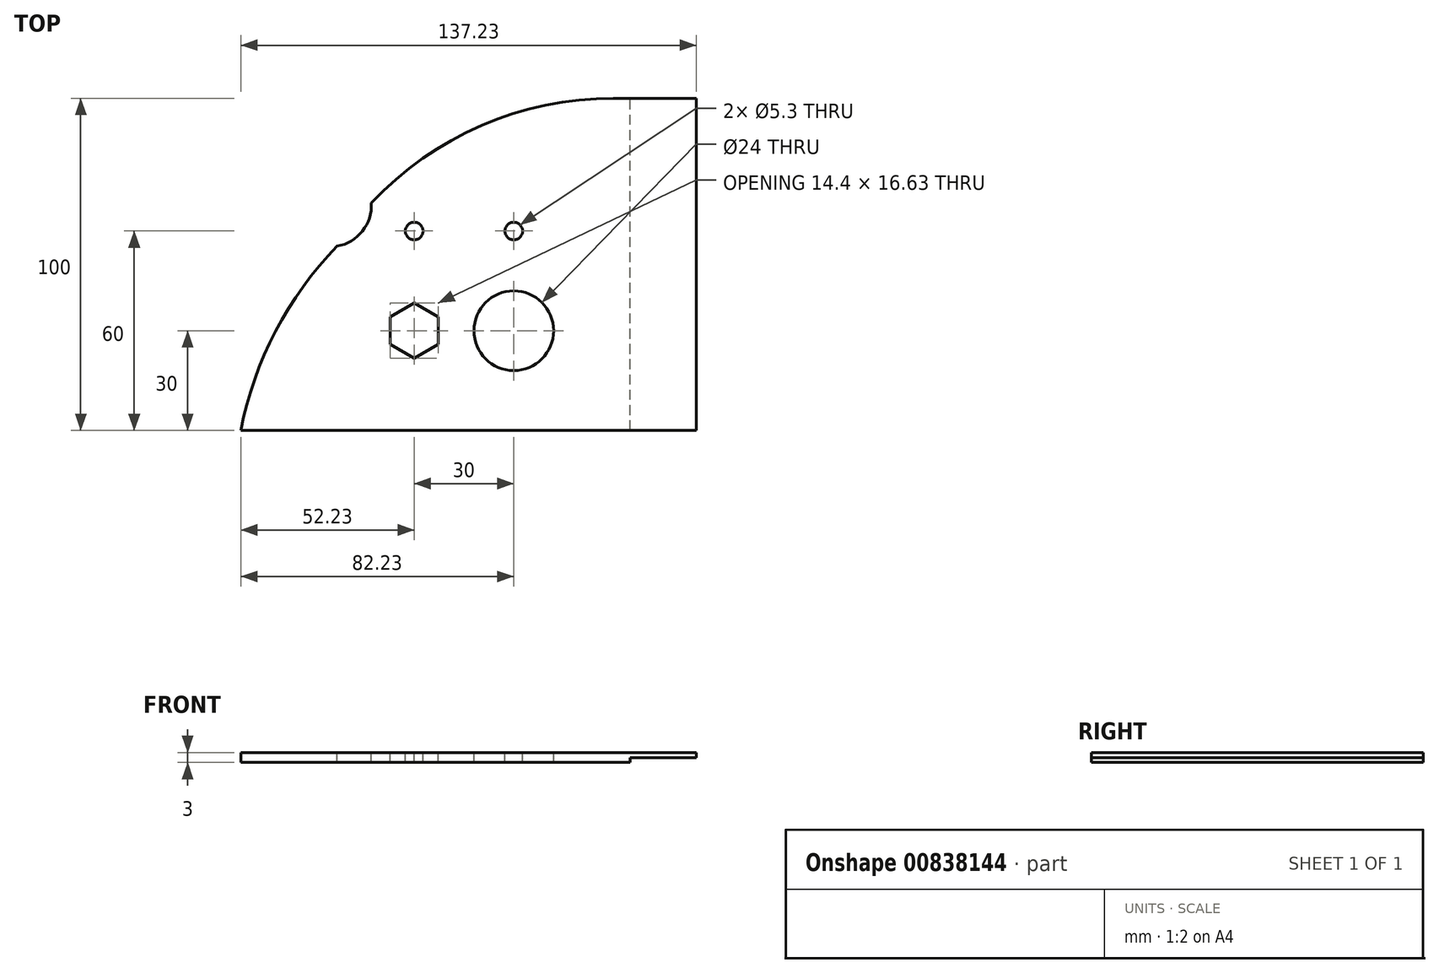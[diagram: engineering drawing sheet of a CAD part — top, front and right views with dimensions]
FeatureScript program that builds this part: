
annotation { "Feature Type Name" : "Feature", "Feature Type Description" : "" }
export const myFeature = defineFeature(function(context is Context, id is Id, definition is map)
    precondition{}
    {
        {
            var Q0;
            Q0=qCreatedBy(makeId("Top.planeOp"),FACE);
            var sketch = newSketch(context, id + "F0", { "sketchPlane" : qUnion([Q0])});
            skLineSegment(sketch, "E0", {"start": v(-202.23, 0) * mm, "end": v(-197.81, 20.8) * mm});
            skLineSegment(sketch, "E1", {"start": v(216.1, 0) * mm, "end": v(-202.23, 0) * mm});
            skLineSegment(sketch, "E2", {"start": v(-100, 100) * mm, "end": v(100, 100) * mm});
            skArc(sketch, "E3", {"start": v(-100, 100) * mm, "mid": v(-162.93, 77.71) * mm, "end": v(-197.81, 20.8) * mm});
            skArc(sketch, "E4", {"start": v(209.29, 20.8) * mm, "mid": v(167.49, 78.12) * mm, "end": v(100, 100) * mm});
            skLineSegment(sketch, "E5", {"start": v(0, 100) * mm, "end": v(0, 0) * mm, "construction": true});
            skLineSegment(sketch, "E6", {"start": v(216.1, 0) * mm, "end": v(209.29, 20.8) * mm});
            skSolve(sketch);
        }
        {
            var Q0;
            Q0=qSketchRegion(id+"F0",true);
            extrude(context, id + "F1", {"entities" : qUnion([Q0]), "depth" : 3 * mm, "offsetDistance" : 25 * mm});
        }
        {
            var Q0;
            Q0=makeQuery(id+"F1.opExtrude","CAP_FACE",FACE,{"disambiguationData":[OSD([sQuery(id+"F0.wireOp",EDGE,"E0"),sQuery(id+"F0.wireOp",EDGE,"E1"),sQuery(id+"F0.wireOp",EDGE,"E2"),sQuery(id+"F0.wireOp",EDGE,"E3"),sQuery(id+"F0.wireOp",EDGE,"E4"),sQuery(id+"F0.wireOp",EDGE,"E6")])],"isStart":false});
            var sketch = newSketch(context, id + "F2", { "sketchPlane" : qUnion([Q0])});
            skCircle(sketch, "E7", {"center": v(0, 12.5) * mm, "radius": 12.6 * mm});
            skLineSegment(sketch, "E8", {"start": v(-11.1, 18.46) * mm, "end": v(-21.76, 0) * mm});
            skLineSegment(sketch, "E9", {"start": v(11.1, 18.46) * mm, "end": v(21.76, 0) * mm});
            skLineSegment(sketch, "E10", {"start": v(21.76, 0) * mm, "end": v(-21.76, 0) * mm});
            skSolve(sketch);
        }
        {
            var Q0;
            Q0=qSketchRegion(id+"F2",true);
            extrude(context, id + "F3", {"entities" : qUnion([Q0]), "operationType" : NewBodyOperationType.REMOVE, "oppositeDirection" : true, "depth" : 25 * mm, "offsetDistance" : 25 * mm});
        }
        {
            var Q0;
            Q0=makeQuery(id+"F3.boolean.opBoolean","COPY",EDGE,{"derivedFrom":makeQuery(id+"F3.opExtrude","SWEPT_EDGE",EDGE,{"disambiguationData":[OSD([sQuery(id+"F0.wireOp",EDGE,"E1"),sQuery(id+"F2.wireOp",EDGE,"E8"),sQuery(id+"F2.wireOp",EDGE,"E10")])]})});
            var Q1;
            Q1=makeQuery(id+"F3.boolean.opBoolean","COPY",EDGE,{"derivedFrom":makeQuery(id+"F3.opExtrude","SWEPT_EDGE",EDGE,{"disambiguationData":[OSD([sQuery(id+"F0.wireOp",EDGE,"E1"),sQuery(id+"F2.wireOp",EDGE,"E9"),sQuery(id+"F2.wireOp",EDGE,"E10")])]})});
            fillet(context, id + "F4", {"entities" : qUnion([Q0, Q1]), "radius" : 5 * mm, "tangentPropagation" : true, "allowEdgeOverflow" : false});
        }
        {
            var Q0;
            Q0=makeQuery(id+"F1.opExtrude","CAP_FACE",FACE,{"disambiguationData":[OSD([sQuery(id+"F0.wireOp",EDGE,"E0"),sQuery(id+"F0.wireOp",EDGE,"E1"),sQuery(id+"F0.wireOp",EDGE,"E2"),sQuery(id+"F0.wireOp",EDGE,"E3"),sQuery(id+"F0.wireOp",EDGE,"E4"),sQuery(id+"F0.wireOp",EDGE,"E6")])],"isStart":false});
            var sketch = newSketch(context, id + "F5", { "sketchPlane" : qUnion([Q0])});
            skCircle(sketch, "E11.cCircle", {"center": v(-160, 30) * mm, "radius": 8.31 * mm, "construction": true});
            skLineSegment(sketch, "E11.0", {"start": v(-167.2, 34.16) * mm, "end": v(-160, 38.31) * mm});
            skLineSegment(sketch, "E11.1", {"start": v(-160, 38.31) * mm, "end": v(-152.8, 34.16) * mm});
            skLineSegment(sketch, "E11.2", {"start": v(-152.8, 34.16) * mm, "end": v(-152.8, 25.84) * mm});
            skLineSegment(sketch, "E11.3", {"start": v(-152.8, 25.84) * mm, "end": v(-160, 21.69) * mm});
            skLineSegment(sketch, "E11.4", {"start": v(-160, 21.69) * mm, "end": v(-167.2, 25.84) * mm});
            skLineSegment(sketch, "E11.5", {"start": v(-167.2, 25.84) * mm, "end": v(-167.2, 34.16) * mm});
            skCircle(sketch, "E12", {"center": v(-130, 30) * mm, "radius": 12 * mm});
            skCircle(sketch, "E13", {"center": v(-130, 60) * mm, "radius": 2.65 * mm});
            skCircle(sketch, "E14", {"center": v(-160, 60) * mm, "radius": 2.65 * mm});
            skSolve(sketch);
        }
        {
            var Q0;
            Q0=qSketchRegion(id+"F5",true);
            extrude(context, id + "F6", {"entities" : qUnion([Q0]), "operationType" : NewBodyOperationType.REMOVE, "oppositeDirection" : true, "depth" : 25 * mm, "offsetDistance" : 25 * mm});
        }
        {
            var Q0;
            Q0=makeQuery(id+"F1.opExtrude","CAP_FACE",FACE,{"disambiguationData":[OSD([sQuery(id+"F0.wireOp",EDGE,"E0"),sQuery(id+"F0.wireOp",EDGE,"E1"),sQuery(id+"F0.wireOp",EDGE,"E2"),sQuery(id+"F0.wireOp",EDGE,"E3"),sQuery(id+"F0.wireOp",EDGE,"E4"),sQuery(id+"F0.wireOp",EDGE,"E6")])],"isStart":false});
            var sketch = newSketch(context, id + "F7", { "sketchPlane" : qUnion([Q0])});
            skLineSegment(sketch, "E15.bottom", {"start": v(-39, 30) * mm, "end": v(39, 30) * mm});
            skLineSegment(sketch, "E15.top", {"start": v(-39, 85.5) * mm, "end": v(39, 85.5) * mm});
            skLineSegment(sketch, "E15.left", {"start": v(-39, 30) * mm, "end": v(-39, 85.5) * mm});
            skLineSegment(sketch, "E15.right", {"start": v(39, 30) * mm, "end": v(39, 85.5) * mm});
            skCircle(sketch, "E16", {"center": v(-42.63, 28.25) * mm, "radius": 2 * mm});
            skCircle(sketch, "E17", {"center": v(-42.63, 87.25) * mm, "radius": 2 * mm});
            skCircle(sketch, "E18", {"center": v(42.37, 87.25) * mm, "radius": 2 * mm});
            skCircle(sketch, "E19", {"center": v(42.37, 28.25) * mm, "radius": 2 * mm});
            skLineSegment(sketch, "E20", {"start": v(0, 85.5) * mm, "end": v(0, 30) * mm, "construction": true});
            skSolve(sketch);
        }
        {
            var Q0;
            Q0=qSketchRegion(id+"F7",true);
            extrude(context, id + "F8", {"entities" : qUnion([Q0]), "operationType" : NewBodyOperationType.REMOVE, "oppositeDirection" : true, "depth" : 25 * mm, "offsetDistance" : 25 * mm});
        }
        {
            var Q0;
            Q0=makeQuery(id+"F1.opExtrude","CAP_FACE",FACE,{"disambiguationData":[OSD([sQuery(id+"F0.wireOp",EDGE,"E0"),sQuery(id+"F0.wireOp",EDGE,"E1"),sQuery(id+"F0.wireOp",EDGE,"E2"),sQuery(id+"F0.wireOp",EDGE,"E3"),sQuery(id+"F0.wireOp",EDGE,"E4"),sQuery(id+"F0.wireOp",EDGE,"E6")])],"isStart":false});
            var sketch = newSketch(context, id + "F9", { "sketchPlane" : qUnion([Q0])});
            skCircle(sketch, "E21", {"center": v(115, 30) * mm, "radius": 8.15 * mm});
            skSolve(sketch);
        }
        {
            var Q0;
            Q0=qSketchRegion(id+"F9",true);
            extrude(context, id + "F10", {"entities" : qUnion([Q0]), "operationType" : NewBodyOperationType.REMOVE, "oppositeDirection" : true, "depth" : 25 * mm, "offsetDistance" : 25 * mm});
        }
        {
            var Q0;
            Q0=makeQuery(id+"F1.opExtrude","CAP_FACE",FACE,{"disambiguationData":[OSD([sQuery(id+"F0.wireOp",EDGE,"E0"),sQuery(id+"F0.wireOp",EDGE,"E1"),sQuery(id+"F0.wireOp",EDGE,"E2"),sQuery(id+"F0.wireOp",EDGE,"E3"),sQuery(id+"F0.wireOp",EDGE,"E4"),sQuery(id+"F0.wireOp",EDGE,"E6")])],"isStart":false});
            var sketch = newSketch(context, id + "F11", { "sketchPlane" : qUnion([Q0])});
            skArc(sketch, "E22", {"start": v(-100, 95) * mm, "mid": v(-155.57, 77.06) * mm, "end": v(-190.14, 30) * mm});
            skPoint(sketch, "E22.endSnap0", {"position": v(-167.2, 30) * mm});
            skLineSegment(sketch, "E23", {"start": v(-100, 95) * mm, "end": v(100, 95) * mm});
            skArc(sketch, "E24", {"start": v(200.37, 30) * mm, "mid": v(159.8, 77.33) * mm, "end": v(100, 95) * mm});
            skSolve(sketch);
        }
        {
            var Q0;
            {var subQ5=sQuery(id+"F0.wireOp",EDGE,"E0");Q0=makeQuery(id+"F11.imprint","IMPRINT",FACE,{"disambiguationData":[TD([[makeQuery(id+"F11.imprint","IMPRINT",EDGE,{"derivedFrom":makeQuery(id+"F1.opExtrude","CAP_EDGE",EDGE,{"disambiguationData":[OSD([subQ5])],"isStart":false})}),-1.0]])]});}
            var sketch = newSketch(context, id + "F12", { "sketchPlane" : qUnion([Q0])});
            skLineSegment(sketch, "E25.bottom", {"start": v(-75, 0) * mm, "end": v(225.73, 0) * mm});
            skLineSegment(sketch, "E25.top", {"start": v(-75, 105.3) * mm, "end": v(225.73, 105.3) * mm});
            skLineSegment(sketch, "E25.left", {"start": v(-75, 0) * mm, "end": v(-75, 105.3) * mm});
            skLineSegment(sketch, "E25.right", {"start": v(225.73, 0) * mm, "end": v(225.73, 105.3) * mm});
            skSolve(sketch);
        }
        {
            var Q0;
            Q0 = qSketchRegion(id + "F12", true);
            extrude(context, id + "F13", {"entities" : qUnion([Q0]), "operationType" : NewBodyOperationType.REMOVE, "oppositeDirection" : true, "depth" : 25 * mm, "offsetDistance" : 25 * mm});
        }
        {
            var Q0;
            Q0=makeQuery(id+"F1.opExtrude","CAP_FACE",FACE,{"disambiguationData":[OSD([sQuery(id+"F0.wireOp",EDGE,"E0"),sQuery(id+"F0.wireOp",EDGE,"E1"),sQuery(id+"F0.wireOp",EDGE,"E2"),sQuery(id+"F0.wireOp",EDGE,"E3"),sQuery(id+"F0.wireOp",EDGE,"E4"),sQuery(id+"F0.wireOp",EDGE,"E6")])],"isStart":true});
            var sketch = newSketch(context, id + "F14", { "sketchPlane" : qUnion([Q0])});
            skLineSegment(sketch, "E26.bottom", {"start": v(-75, 0) * mm, "end": v(-95, 0) * mm});
            skLineSegment(sketch, "E26.top", {"start": v(-75, -100) * mm, "end": v(-95, -100) * mm});
            skLineSegment(sketch, "E26.left", {"start": v(-75, 0) * mm, "end": v(-75, -100) * mm});
            skLineSegment(sketch, "E26.right", {"start": v(-95, 0) * mm, "end": v(-95, -100) * mm});
            skSolve(sketch);
        }
        {
            var Q0;
            Q0 = qSketchRegion(id + "F14", true);
            extrude(context, id + "F15", {"entities" : qUnion([Q0]), "operationType" : NewBodyOperationType.REMOVE, "oppositeDirection" : true, "depth" : 1.5 * mm, "offsetDistance" : 25 * mm});
        }
        {
            var Q0;
            {var subQ5=sQuery(id+"F0.wireOp",EDGE,"E0");Q0=makeQuery(id+"F11.imprint","IMPRINT",FACE,{"disambiguationData":[TD([[makeQuery(id+"F11.imprint","IMPRINT",EDGE,{"derivedFrom":makeQuery(id+"F1.opExtrude","CAP_EDGE",EDGE,{"disambiguationData":[OSD([subQ5])],"isStart":false})}),-1.0]])]});}
            var sketch = newSketch(context, id + "F16", { "sketchPlane" : qUnion([Q0])});
            skCircle(sketch, "E27", {"center": v(-185.39, 67.75) * mm, "radius": 12.5 * mm});
            skSolve(sketch);
        }
        {
            var Q0;
            {var subQ0=sQuery(id+"F16.wireOp",EDGE,"E27");var subQ1=makeQuery(id+"F11.imprint","IMPRINT",EDGE,{"derivedFrom":makeQuery(id+"F1.opExtrude","CAP_EDGE",EDGE,{"disambiguationData":[OSD([sQuery(id+"F0.wireOp",EDGE,"E3")])],"isStart":false})});var subQ2=makeQuery(id+"F16.imprint","INTERSECT",VERTEX,{"disambiguationData":[OD(0.0)],"derivedFrom":[subQ1,subQ0]});Q0=makeQuery(id+"F16.imprint","IMPRINT",FACE,{"disambiguationData":[TD([[makeQuery(id+"F16.imprint","IMPRINT",EDGE,{"disambiguationData":[TD([[subQ2,1.0]])],"derivedFrom":subQ0}),1.0]])]});}
            var Q1;
            {var subQ0=sQuery(id+"F16.wireOp",EDGE,"E27");var subQ1=makeQuery(id+"F11.imprint","IMPRINT",EDGE,{"derivedFrom":makeQuery(id+"F1.opExtrude","CAP_EDGE",EDGE,{"disambiguationData":[OSD([sQuery(id+"F0.wireOp",EDGE,"E3")])],"isStart":false})});var subQ2=makeQuery(id+"F16.imprint","INTERSECT",VERTEX,{"disambiguationData":[OD(0.0)],"derivedFrom":[subQ1,subQ0]});Q1=makeQuery(id+"F16.imprint","IMPRINT",FACE,{"disambiguationData":[TD([[makeQuery(id+"F16.imprint","IMPRINT",EDGE,{"disambiguationData":[TD([[subQ2,-1.0]])],"derivedFrom":subQ0}),1.0]])]});}
            extrude(context, id + "F17", {"entities" : qUnion([Q0, Q1]), "operationType" : NewBodyOperationType.REMOVE, "oppositeDirection" : true, "depth" : 25 * mm, "offsetDistance" : 25 * mm});
        }
        {
            var Q0;
            {var subQ5=sQuery(id+"F0.wireOp",EDGE,"E0");Q0=makeQuery(id+"F11.imprint","IMPRINT",FACE,{"disambiguationData":[TD([[makeQuery(id+"F11.imprint","IMPRINT",EDGE,{"derivedFrom":makeQuery(id+"F1.opExtrude","CAP_EDGE",EDGE,{"disambiguationData":[OSD([subQ5])],"isStart":false})}),-1.0]])]});}
            var sketch = newSketch(context, id + "F18", { "sketchPlane" : qUnion([Q0])});
            skPoint(sketch, "E28.0", {"position": v(-183.23, 55.44) * mm});
            skArc(sketch, "E29", {"start": v(-183.23, 55.44) * mm, "mid": v(-201.75, 29.83) * mm, "end": v(-212.23, 0) * mm});
            skLineSegment(sketch, "E30", {"start": v(-212.23, 0) * mm, "end": v(-183.23, 0) * mm});
            skLineSegment(sketch, "E31", {"start": v(-183.23, 0) * mm, "end": v(-183.23, 55.44) * mm});
            skSolve(sketch);
        }
        {
            var Q0;
            Q0 = qSketchRegion(id + "F18", true);
            extrude(context, id + "F19", {"entities" : qUnion([Q0]), "operationType" : NewBodyOperationType.ADD, "oppositeDirection" : true, "depth" : 3 * mm, "offsetDistance" : 25 * mm});
        }
    });
